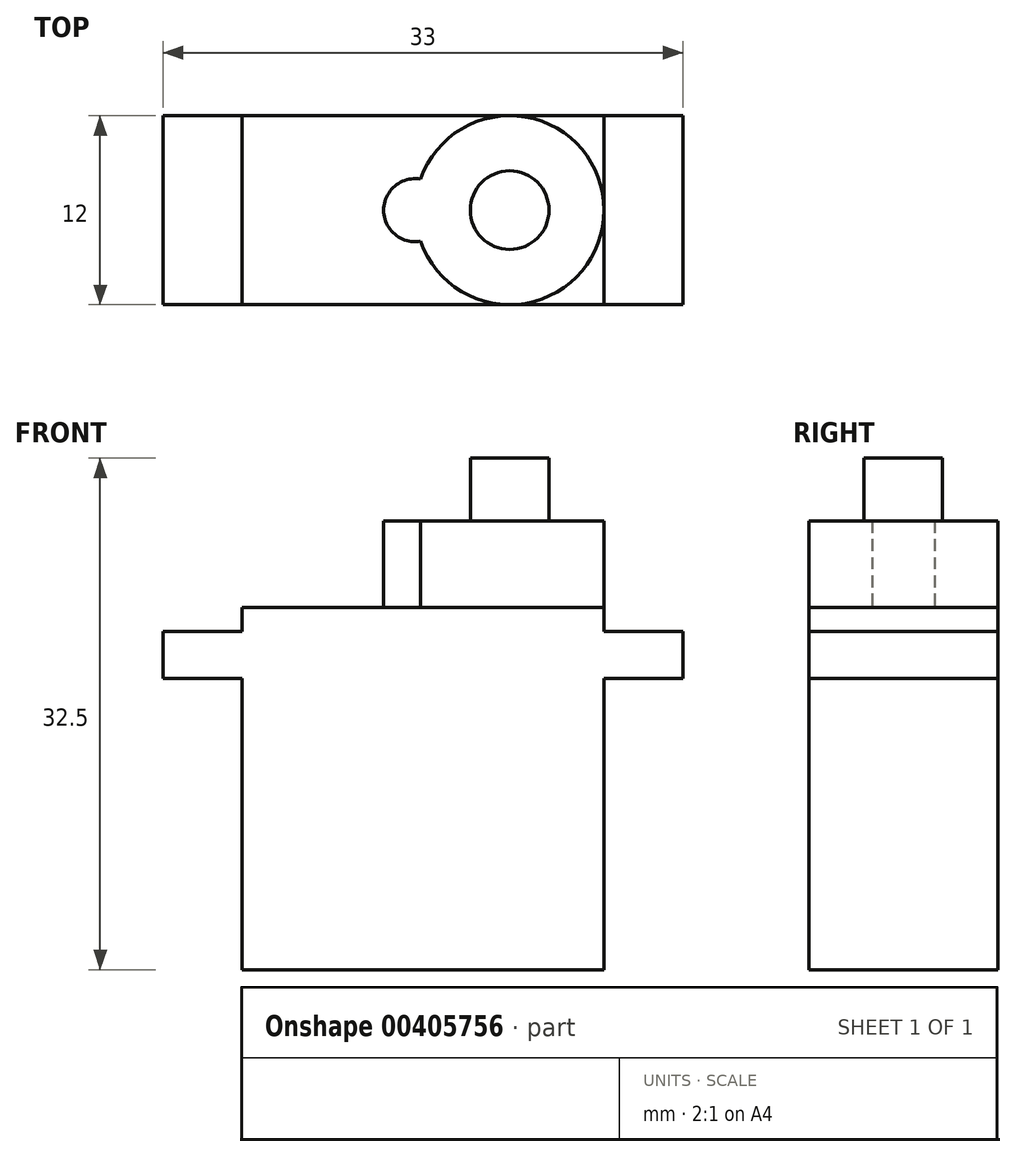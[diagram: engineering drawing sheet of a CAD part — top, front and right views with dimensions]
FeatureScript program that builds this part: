
annotation { "Feature Type Name" : "Feature", "Feature Type Description" : "" }
export const myFeature = defineFeature(function(context is Context, id is Id, definition is map)
    precondition{}
    {
        {
            var Q0;
            Q0=qCreatedBy(makeId("Top.planeOp"),FACE);
            var sketch = newSketch(context, id + "F0", { "sketchPlane" : qUnion([Q0])});
            skLineSegment(sketch, "E0.bottom", {"start": v(-11.5, 6) * mm, "end": v(11.5, 6) * mm});
            skLineSegment(sketch, "E0.top", {"start": v(-11.5, -6) * mm, "end": v(11.5, -6) * mm});
            skLineSegment(sketch, "E0.left", {"start": v(-11.5, 6) * mm, "end": v(-11.5, -6) * mm});
            skLineSegment(sketch, "E0.right", {"start": v(11.5, 6) * mm, "end": v(11.5, -6) * mm});
            skLineSegment(sketch, "E1", {"start": v(-11.5, 6) * mm, "end": v(11.5, -6) * mm, "construction": true});
            skPoint(sketch, "E2", {"position": v(0, 0) * mm});
            skSolve(sketch);
        }
        {
            var Q0;
            Q0=makeQuery(id+"F0.imprint","IMPRINT",FACE,{"disambiguationData":[TD([[makeQuery(id+"F0.imprint","IMPRINT",EDGE,{"derivedFrom":sQuery(id+"F0.wireOp",EDGE,"E0.bottom")}),-1.0]])]});
            extrude(context, id + "F1", {"entities" : qUnion([Q0]), "endBound" : BoundingType.SYMMETRIC, "depth" : 23 * mm});
        }
        {
            var Q0;
            Q0=makeQuery(id+"F1.opExtrude","CAP_FACE",FACE,{"disambiguationData":[OSD([sQuery(id+"F0.wireOp",EDGE,"E0.bottom"),sQuery(id+"F0.wireOp",EDGE,"E0.top"),sQuery(id+"F0.wireOp",EDGE,"E0.left"),sQuery(id+"F0.wireOp",EDGE,"E0.right")])],"isStart":false});
            var sketch = newSketch(context, id + "F2", { "sketchPlane" : qUnion([Q0])});
            skCircle(sketch, "E3", {"center": v(5.5, 0) * mm, "radius": 6 * mm});
            skCircle(sketch, "E4", {"center": v(-0.5, 0) * mm, "radius": 2 * mm});
            skSolve(sketch);
        }
        {
            var Q0;
            Q0=makeQuery(id+"F2.imprint","IMPRINT",FACE,{"disambiguationData":[TD([[makeQuery(id+"F2.imprint","IMPRINT",EDGE,{"derivedFrom":sQuery(id+"F2.wireOp",EDGE,"E3")}),1.0]])]});
            var Q1;
            {var subQ0=sQuery(id+"F2.wireOp",EDGE,"E4");var subQ1=sQuery(id+"F2.wireOp",EDGE,"E3");var subQ2=makeQuery(id+"F2.imprint","INTERSECT",VERTEX,{"disambiguationData":[OD(0.0)],"derivedFrom":[subQ1,subQ0]});Q1=makeQuery(id+"F2.imprint","IMPRINT",FACE,{"disambiguationData":[TD([[makeQuery(id+"F2.imprint","IMPRINT",EDGE,{"disambiguationData":[TD([[subQ2,-1.0]])],"derivedFrom":subQ1}),1.0]])]});}
            var Q2;
            {var subQ0=sQuery(id+"F2.wireOp",EDGE,"E4");var subQ1=sQuery(id+"F2.wireOp",EDGE,"E3");var subQ2=makeQuery(id+"F2.imprint","INTERSECT",VERTEX,{"disambiguationData":[OD(0.0)],"derivedFrom":[subQ1,subQ0]});Q2=makeQuery(id+"F2.imprint","IMPRINT",FACE,{"disambiguationData":[TD([[makeQuery(id+"F2.imprint","IMPRINT",EDGE,{"disambiguationData":[TD([[subQ2,-1.0]])],"derivedFrom":subQ1}),-1.0]])]});}
            extrude(context, id + "F3", {"entities" : qUnion([Q0, Q1, Q2]), "operationType" : NewBodyOperationType.ADD, "depth" : 5.5 * mm});
        }
        {
            var Q0;
            Q0=makeQuery(id+"F3.opExtrude","CAP_FACE",FACE,{"disambiguationData":[OSD([sQuery(id+"F2.wireOp",EDGE,"E3"),sQuery(id+"F2.wireOp",EDGE,"E4")])],"isStart":false});
            var sketch = newSketch(context, id + "F4", { "sketchPlane" : qUnion([Q0])});
            skCircle(sketch, "E5", {"center": v(5.5, 0) * mm, "radius": 2.5 * mm});
            skSolve(sketch);
        }
        {
            var Q0;
            Q0=makeQuery(id+"F4.imprint","IMPRINT",FACE,{"disambiguationData":[TD([[makeQuery(id+"F4.imprint","IMPRINT",EDGE,{"derivedFrom":sQuery(id+"F4.wireOp",EDGE,"E5")}),1.0]])]});
            extrude(context, id + "F5", {"entities" : qUnion([Q0]), "operationType" : NewBodyOperationType.ADD, "depth" : 4 * mm});
        }
        {
            var Q0;
            Q0=makeQuery(id+"F1.opExtrude","SWEPT_FACE",FACE,{"disambiguationData":[OSD([sQuery(id+"F0.wireOp",EDGE,"E0.top")])]});
            var sketch = newSketch(context, id + "F6", { "sketchPlane" : qUnion([Q0])});
            skLineSegment(sketch, "E6.bottom", {"start": v(-11.5, 7) * mm, "end": v(-16.5, 7) * mm});
            skLineSegment(sketch, "E6.top", {"start": v(-11.5, 10) * mm, "end": v(-16.5, 10) * mm});
            skLineSegment(sketch, "E6.left", {"start": v(-11.5, 7) * mm, "end": v(-11.5, 10) * mm});
            skLineSegment(sketch, "E6.right", {"start": v(-16.5, 7) * mm, "end": v(-16.5, 10) * mm});
            skLineSegment(sketch, "E7.bottom", {"start": v(11.5, 7) * mm, "end": v(16.5, 7) * mm});
            skLineSegment(sketch, "E7.top", {"start": v(11.5, 10) * mm, "end": v(16.5, 10) * mm});
            skLineSegment(sketch, "E7.left", {"start": v(11.5, 7) * mm, "end": v(11.5, 10) * mm});
            skLineSegment(sketch, "E7.right", {"start": v(16.5, 7) * mm, "end": v(16.5, 10) * mm});
            skSolve(sketch);
        }
        {
            var Q0;
            Q0=makeQuery(id+"F6.imprint","IMPRINT",FACE,{"disambiguationData":[TD([[makeQuery(id+"F6.imprint","IMPRINT",EDGE,{"derivedFrom":sQuery(id+"F6.wireOp",EDGE,"E6.bottom")}),-1.0]])]});
            var Q1;
            Q1=makeQuery(id+"F6.imprint","IMPRINT",FACE,{"disambiguationData":[TD([[makeQuery(id+"F6.imprint","IMPRINT",EDGE,{"derivedFrom":sQuery(id+"F6.wireOp",EDGE,"E7.bottom")}),1.0]])]});
            extrude(context, id + "F7", {"entities" : qUnion([Q0, Q1]), "operationType" : NewBodyOperationType.ADD, "oppositeDirection" : true, "depth" : 12 * mm});
        }
    });
